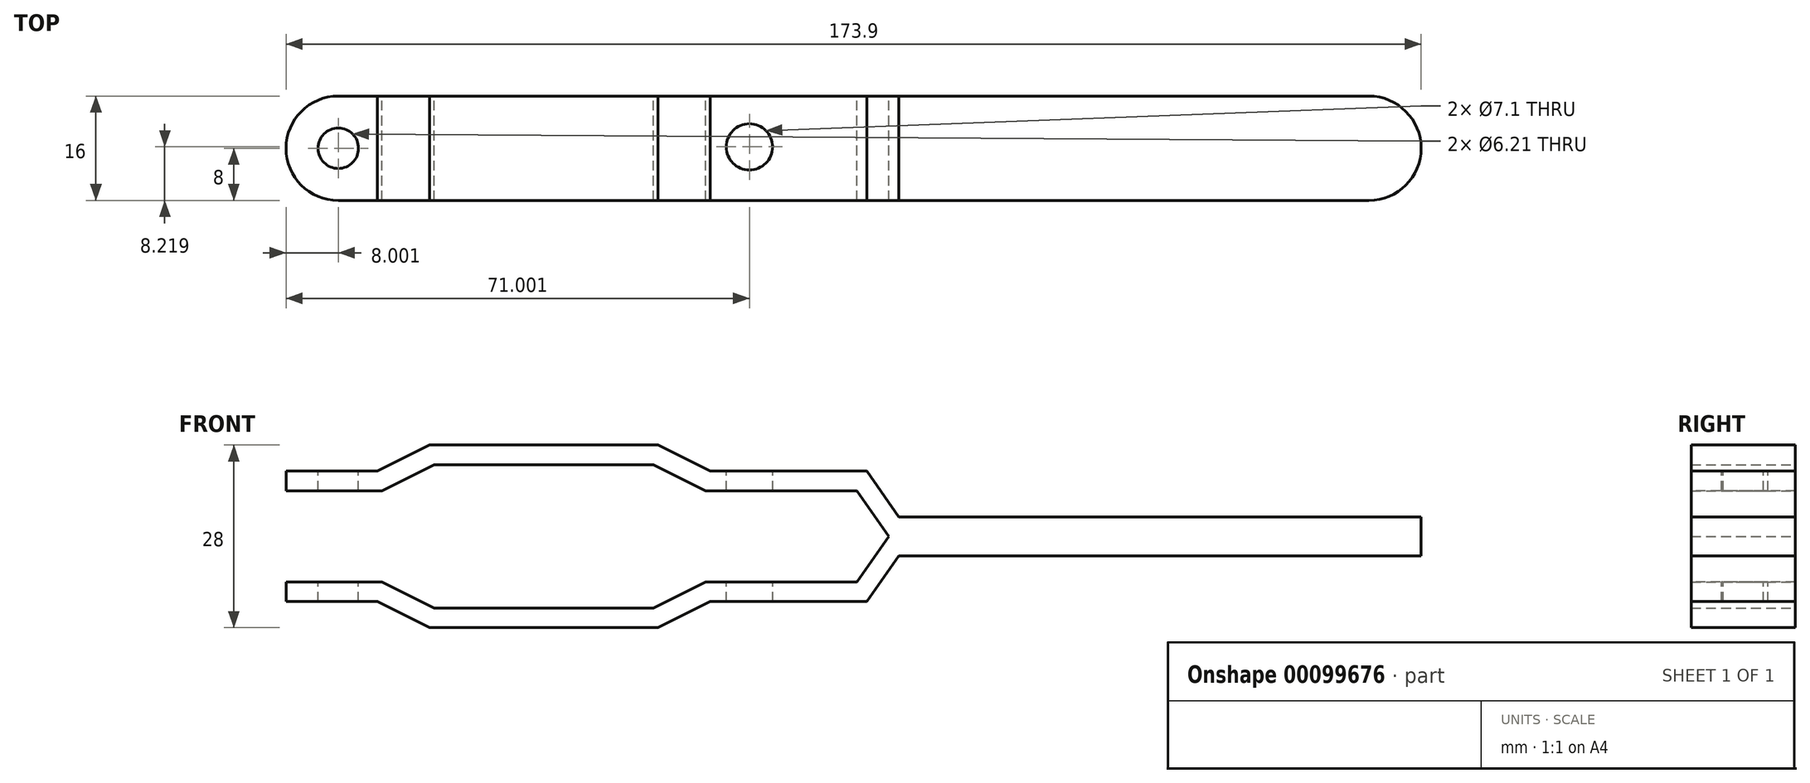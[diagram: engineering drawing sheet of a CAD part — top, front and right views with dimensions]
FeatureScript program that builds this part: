
annotation { "Feature Type Name" : "Feature", "Feature Type Description" : "" }
export const myFeature = defineFeature(function(context is Context, id is Id, definition is map)
    precondition{}
    {
        {
            var Q0;
            Q0=qCreatedBy(makeId("Front.planeOp"),FACE);
            var sketch = newSketch(context, id + "F0", { "sketchPlane" : qUnion([Q0])});
            skLineSegment(sketch, "E0", {"start": v(-64.2, 0) * mm, "end": v(31.8, 0) * mm});
            skLineSegment(sketch, "E1", {"start": v(-64.2, 0) * mm, "end": v(-64.2, -10) * mm});
            skLineSegment(sketch, "E2", {"start": v(-64.2, -10) * mm, "end": v(-50.2, -10) * mm});
            skLineSegment(sketch, "E3", {"start": v(-50.2, -10) * mm, "end": v(-42.2, -14) * mm});
            skLineSegment(sketch, "E4", {"start": v(-42.2, -14) * mm, "end": v(-7.2, -14) * mm});
            skLineSegment(sketch, "E5", {"start": v(-7.2, -14) * mm, "end": v(0.8, -10) * mm});
            skLineSegment(sketch, "E6", {"start": v(0.8, -10) * mm, "end": v(24.8, -10) * mm});
            skLineSegment(sketch, "E7.MirrorCS", {"start": v(-64.2, 10) * mm, "end": v(-50.2, 10) * mm});
            skLineSegment(sketch, "E8.MirrorCS", {"start": v(-50.2, 10) * mm, "end": v(-42.2, 14) * mm});
            skLineSegment(sketch, "E9.MirrorCS", {"start": v(-42.2, 14) * mm, "end": v(-7.2, 14) * mm});
            skLineSegment(sketch, "E10.MirrorCS", {"start": v(-7.2, 14) * mm, "end": v(0.8, 10) * mm});
            skLineSegment(sketch, "E11.MirrorCS", {"start": v(0.8, 10) * mm, "end": v(24.8, 10) * mm});
            skLineSegment(sketch, "E12.MirrorCS", {"start": v(-64.2, 0) * mm, "end": v(-64.2, 10) * mm});
            skLineSegment(sketch, "E13", {"start": v(24.8, -10) * mm, "end": v(31.8, 0) * mm});
            skLineSegment(sketch, "E14", {"start": v(31.8, 0) * mm, "end": v(24.8, 10) * mm});
            skLineSegment(sketch, "E15", {"start": v(29.7, 3) * mm, "end": v(109.7, 3) * mm});
            skLineSegment(sketch, "E16", {"start": v(109.7, 3) * mm, "end": v(109.7, -3) * mm});
            skLineSegment(sketch, "E17", {"start": v(109.7, -3) * mm, "end": v(29.7, -3) * mm});
            skSolve(sketch);
        }
        {
            var Q0;
            Q0 = qSketchRegion(id + "F0", true);
            extrude(context, id + "F1", {"entities" : qUnion([Q0]), "depth" : 16 * mm});
        }
        {
            var Q0;
            Q0=makeQuery(id+"F1.opExtrude","CAP_FACE",FACE,{"disambiguationData":[OSD([sQuery(id+"F0.wireOp",EDGE,"E1"),sQuery(id+"F0.wireOp",EDGE,"E2"),sQuery(id+"F0.wireOp",EDGE,"E3"),sQuery(id+"F0.wireOp",EDGE,"E4"),sQuery(id+"F0.wireOp",EDGE,"E5"),sQuery(id+"F0.wireOp",EDGE,"E6"),sQuery(id+"F0.wireOp",EDGE,"E7.MirrorCS"),sQuery(id+"F0.wireOp",EDGE,"E8.MirrorCS"),sQuery(id+"F0.wireOp",EDGE,"E9.MirrorCS"),sQuery(id+"F0.wireOp",EDGE,"E10.MirrorCS"),sQuery(id+"F0.wireOp",EDGE,"E11.MirrorCS"),sQuery(id+"F0.wireOp",EDGE,"E12.MirrorCS"),sQuery(id+"F0.wireOp",EDGE,"E13"),sQuery(id+"F0.wireOp",EDGE,"E14")])],"isStart":true});
            var Q1;
            Q1=makeQuery(id+"F1.opExtrude","CAP_FACE",FACE,{"disambiguationData":[OSD([sQuery(id+"F0.wireOp",EDGE,"E1"),sQuery(id+"F0.wireOp",EDGE,"E2"),sQuery(id+"F0.wireOp",EDGE,"E3"),sQuery(id+"F0.wireOp",EDGE,"E4"),sQuery(id+"F0.wireOp",EDGE,"E5"),sQuery(id+"F0.wireOp",EDGE,"E6"),sQuery(id+"F0.wireOp",EDGE,"E7.MirrorCS"),sQuery(id+"F0.wireOp",EDGE,"E8.MirrorCS"),sQuery(id+"F0.wireOp",EDGE,"E9.MirrorCS"),sQuery(id+"F0.wireOp",EDGE,"E10.MirrorCS"),sQuery(id+"F0.wireOp",EDGE,"E11.MirrorCS"),sQuery(id+"F0.wireOp",EDGE,"E12.MirrorCS"),sQuery(id+"F0.wireOp",EDGE,"E13"),sQuery(id+"F0.wireOp",EDGE,"E14")])],"isStart":false});
            var Q2;
            Q2=makeQuery(id+"F1.opExtrude","SWEPT_FACE",FACE,{"disambiguationData":[OSD([sQuery(id+"F0.wireOp",EDGE,"E1"),sQuery(id+"F0.wireOp",EDGE,"E12.MirrorCS")])]});
            shell(context, id + "F2", {"entities" : qUnion([Q0, Q1, Q2]), "thickness" : 3 * mm});
        }
        {
            var Q0;
            Q0=makeQuery(id+"F1.opExtrude","CAP_EDGE",EDGE,{"disambiguationData":[OSD([sQuery(id+"F0.wireOp",EDGE,"E1"),sQuery(id+"F0.wireOp",EDGE,"E12.MirrorCS")])],"isStart":false});
            var Q1;
            Q1=makeQuery(id+"F1.opExtrude","CAP_EDGE",EDGE,{"disambiguationData":[OSD([sQuery(id+"F0.wireOp",EDGE,"E1"),sQuery(id+"F0.wireOp",EDGE,"E12.MirrorCS")])],"isStart":true});
            var Q2;
            {var subQ0=sQuery(id+"F0.wireOp",EDGE,"E12.MirrorCS");var subQ1=sQuery(id+"F0.wireOp",EDGE,"E1");Q2=makeQuery(id+"F2.opShell","OFFSET_EDGE",EDGE,{"disambiguationData":[OSD([subQ1,subQ0]),TDD([makeQuery(id+"F1.opExtrude","CAP_EDGE",EDGE,{"disambiguationData":[OSD([subQ1,subQ0])],"isStart":false})])]});}
            var Q3;
            {var subQ0=sQuery(id+"F0.wireOp",EDGE,"E12.MirrorCS");var subQ1=sQuery(id+"F0.wireOp",EDGE,"E1");Q3=makeQuery(id+"F2.opShell","OFFSET_EDGE",EDGE,{"disambiguationData":[OSD([subQ1,subQ0]),TDD([makeQuery(id+"F1.opExtrude","CAP_EDGE",EDGE,{"disambiguationData":[OSD([subQ1,subQ0])],"isStart":true})])]});}
            var Q4;
            Q4=makeQuery(id+"F1.opExtrude","CAP_EDGE",EDGE,{"disambiguationData":[OSD([sQuery(id+"F0.wireOp",EDGE,"E16")])],"isStart":false});
            var Q5;
            Q5=makeQuery(id+"F1.opExtrude","CAP_EDGE",EDGE,{"disambiguationData":[OSD([sQuery(id+"F0.wireOp",EDGE,"E16")])],"isStart":true});
            fillet(context, id + "F3", {"entities" : qUnion([Q0, Q1, Q2, Q3, Q4, Q5]), "radius" : 8 * mm, "tangentPropagation" : true, "allowEdgeOverflow" : false});
        }
        {
            var Q0;
            Q0=makeQuery(id+"F1.opExtrude","SWEPT_FACE",FACE,{"disambiguationData":[OSD([sQuery(id+"F0.wireOp",EDGE,"E7.MirrorCS")])]});
            var sketch = newSketch(context, id + "F4", { "sketchPlane" : qUnion([Q0])});
            skCircle(sketch, "E18", {"center": v(-56.2, -8) * mm, "radius": 3.1 * mm});
            skCircle(sketch, "E19", {"center": v(6.8, -7.78) * mm, "radius": 3.55 * mm});
            skSolve(sketch);
        }
        {
            var Q0;
            Q0 = qSketchRegion(id + "F4", true);
            extrude(context, id + "F5", {"entities" : qUnion([Q0]), "operationType" : NewBodyOperationType.REMOVE, "oppositeDirection" : true, "depth" : 20 * mm});
        }
    });
